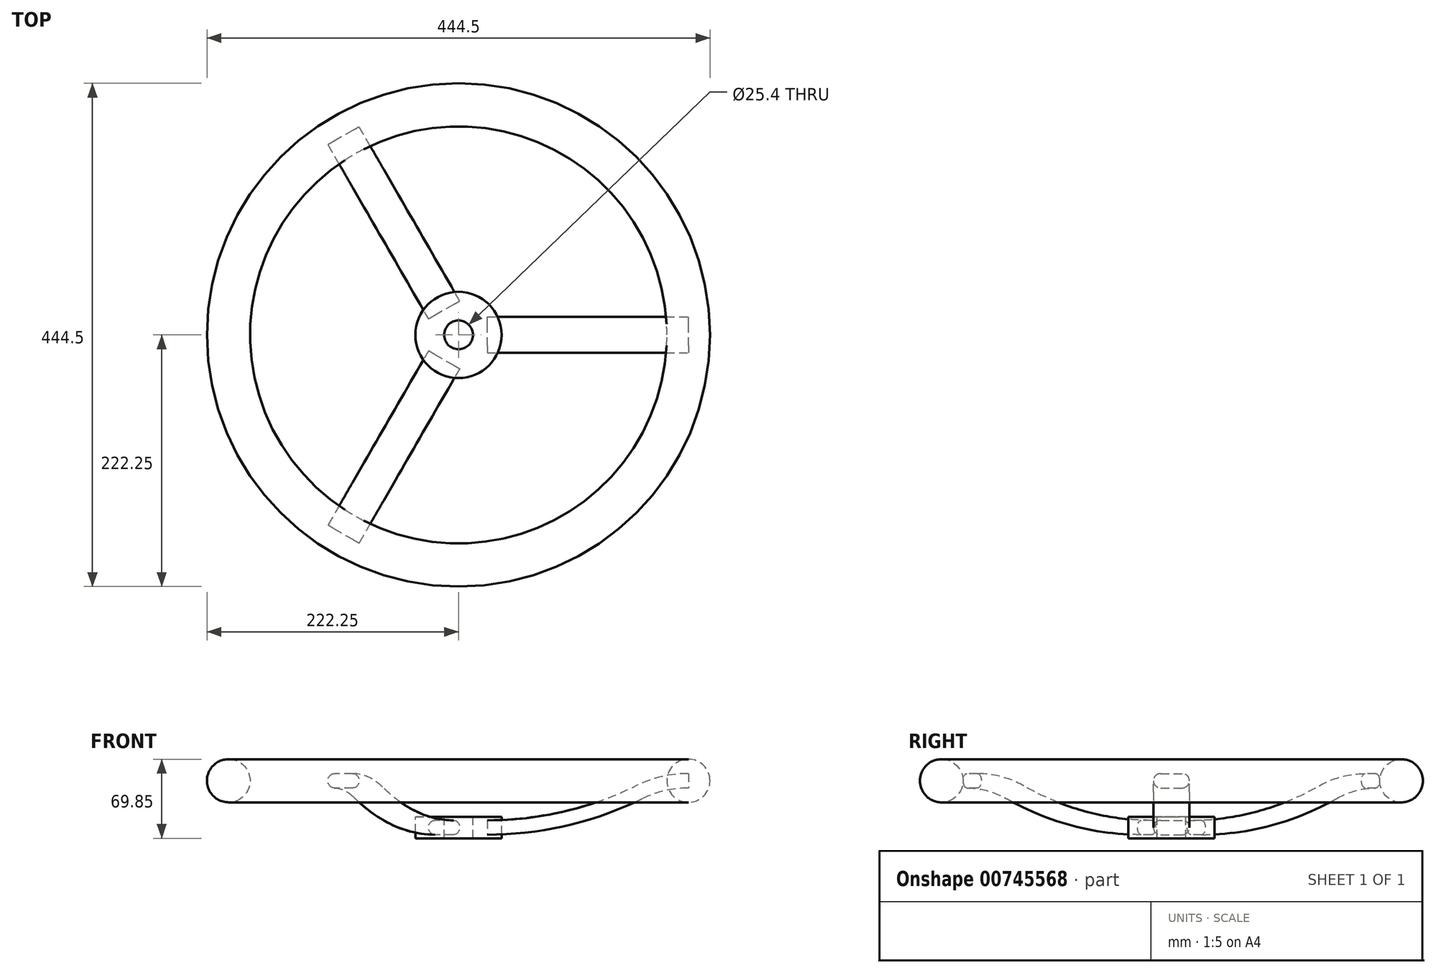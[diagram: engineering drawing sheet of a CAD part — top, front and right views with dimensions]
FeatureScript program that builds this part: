
annotation { "Feature Type Name" : "Feature", "Feature Type Description" : "" }
export const myFeature = defineFeature(function(context is Context, id is Id, definition is map)
    precondition{}
    {
        {
            var Q0;
            Q0=qCreatedBy(makeId("Front.planeOp"),FACE);
            var sketch = newSketch(context, id + "F0", { "sketchPlane" : qUnion([Q0])});
            skLineSegment(sketch, "E0.bottom", {"start": v(0, 0) * mm, "end": v(203.2, 0) * mm, "construction": true});
            skLineSegment(sketch, "E0.top", {"start": v(0, -50.8) * mm, "end": v(203.2, -50.8) * mm, "construction": true});
            skLineSegment(sketch, "E0.left", {"start": v(0, 0) * mm, "end": v(0, -50.8) * mm, "construction": true});
            skLineSegment(sketch, "E0.right", {"start": v(203.2, 0) * mm, "end": v(203.2, -50.8) * mm, "construction": true});
            skCircle(sketch, "E1", {"center": v(203.2, 0) * mm, "radius": 19.05 * mm});
            skLineSegment(sketch, "E2.bottom", {"start": v(38.1, -50.8) * mm, "end": v(12.7, -50.8) * mm});
            skLineSegment(sketch, "E2.top", {"start": v(38.1, -31.75) * mm, "end": v(12.7, -31.75) * mm});
            skLineSegment(sketch, "E2.left", {"start": v(38.1, -50.8) * mm, "end": v(38.1, -31.75) * mm});
            skLineSegment(sketch, "E2.right", {"start": v(12.7, -50.8) * mm, "end": v(12.7, -31.75) * mm});
            skPoint(sketch, "E2.middle", {"position": v(25.4, -41.27) * mm});
            skLineSegment(sketch, "E3", {"start": v(25.4, -41.27) * mm, "end": v(144.92, -41.27) * mm, "construction": true});
            skArc(sketch, "E4", {"start": v(25.4, -41.28) * mm, "mid": v(94.32, -33.38) * mm, "end": v(159.68, -10.1) * mm});
            skArc(sketch, "E5", {"start": v(203.2, 0) * mm, "mid": v(180.86, -2.56) * mm, "end": v(159.68, -10.1) * mm});
            skSolve(sketch);
        }
        {
            var Q0;
            Q0=sQuery(id+"F0.wireOp",EDGE,"E0.bottom");
            var Q1;
            Q1=sQuery(id+"F0.wireOp",VERTEX,"E5.start");
            cPlane(context, id + "F1", {"entities" : qUnion([Q0, Q1]), "cplaneType" : CPlaneType.LINE_POINT, "offset" : 25.4 * mm, "width" : 152.4 * mm, "height" : 152.4 * mm});
        }
        {
            var Q0;
            Q0=makeQuery(id+"F0.imprint","IMPRINT",FACE,{"disambiguationData":[TD([[makeQuery(id+"F0.imprint","IMPRINT",EDGE,{"derivedFrom":sQuery(id+"F0.wireOp",EDGE,"E1")}),1.0]])]});
            var Q1;
            {var subQ3=sQuery(id+"F0.wireOp",EDGE,"E2.bottom");Q1=makeQuery(id+"F0.imprint","IMPRINT",FACE,{"disambiguationData":[TD([[makeQuery(id+"F0.imprint","IMPRINT",EDGE,{"derivedFrom":subQ3}),-1.0]])]});}
            var Q2;
            Q2=sQuery(id+"F0.wireOp",EDGE,"E0.left");
            revolve(context, id + "F2", {"surfaceOperationType" : NewSurfaceOperationType.NEW, "entities" : qUnion([Q0, Q1]), "axis" : qUnion([Q2]), "revolveType" : RevolveType.FULL});
        }
        {
            var Q0;
            Q0=qCreatedBy(id+"F1.planeOp",FACE);
            var sketch = newSketch(context, id + "F3", { "sketchPlane" : qUnion([Q0])});
            skLineSegment(sketch, "E6.bottom", {"start": v(-9.53, -6.35) * mm, "end": v(9.52, -6.35) * mm});
            skLineSegment(sketch, "E6.top", {"start": v(-9.52, 6.35) * mm, "end": v(9.53, 6.35) * mm});
            skLineSegment(sketch, "E6.left", {"start": v(-15.88, 0) * mm, "end": v(-15.88, 0) * mm});
            skLineSegment(sketch, "E6.right", {"start": v(15.88, 0) * mm, "end": v(15.88, 0) * mm});
            skPoint(sketch, "E6.middle", {"position": v(0, 0) * mm});
            skPoint(sketch, "E7.visualSharp", {"position": v(-15.88, -6.35) * mm});
            skArc(sketch, "E7.filletArc", {"start": v(-15.88, 0) * mm, "mid": v(-14.02, -4.5) * mm, "end": v(-9.53, -6.35) * mm});
            skPoint(sketch, "E8.visualSharp", {"position": v(-15.88, 6.35) * mm});
            skArc(sketch, "E8.filletArc", {"start": v(-9.52, 6.35) * mm, "mid": v(-14.02, 4.5) * mm, "end": v(-15.88, 0) * mm});
            skPoint(sketch, "E9.visualSharp", {"position": v(15.87, 6.35) * mm});
            skArc(sketch, "E9.filletArc", {"start": v(15.88, 0) * mm, "mid": v(14.02, 4.5) * mm, "end": v(9.53, 6.35) * mm});
            skPoint(sketch, "E10.visualSharp", {"position": v(15.88, -6.35) * mm});
            skArc(sketch, "E10.filletArc", {"start": v(9.52, -6.35) * mm, "mid": v(14.02, -4.5) * mm, "end": v(15.88, 0) * mm});
            skSolve(sketch);
        }
        {
            var Q0;
            Q0=makeQuery(id+"F3.imprint","IMPRINT",FACE,{"disambiguationData":[TD([[makeQuery(id+"F3.imprint","IMPRINT",EDGE,{"derivedFrom":sQuery(id+"F3.wireOp",EDGE,"E6.bottom")}),1.0]])]});
            var Q1;
            Q1=sQuery(id+"F0.wireOp",EDGE,"E5");
            var Q2;
            Q2=sQuery(id+"F0.wireOp",EDGE,"E4");
            sweep(context, id + "F4", {"profiles" : qUnion([Q0]), "path" : qUnion([Q1, Q2])});
        }
        {
            var Q0;
            Q0=makeQuery(id+"F4.opSweep","SWEPT_BODY",BODY,{"disambiguationData":[OSD([sQuery(id+"F0.wireOp",EDGE,"E4"),sQuery(id+"F3.wireOp",EDGE,"E6.bottom"),sQuery(id+"F3.wireOp",EDGE,"E6.top"),sQuery(id+"F3.wireOp",EDGE,"E7.filletArc"),sQuery(id+"F3.wireOp",EDGE,"E8.filletArc"),sQuery(id+"F3.wireOp",EDGE,"E9.filletArc"),sQuery(id+"F3.wireOp",EDGE,"E10.filletArc")])]});
            var Q1;
            Q1=makeQuery(id+"F2.opRevolve","SWEPT_FACE",FACE,{"disambiguationData":[OSD([sQuery(id+"F0.wireOp",EDGE,"E1")])]});
            circularPattern(context, id + "F5", {"entities" : qUnion([Q0]), "axis" : qUnion([Q1]), "angle" : 360 * degree, "instanceCount" : 3, "equalSpace" : true});
        }
    });
